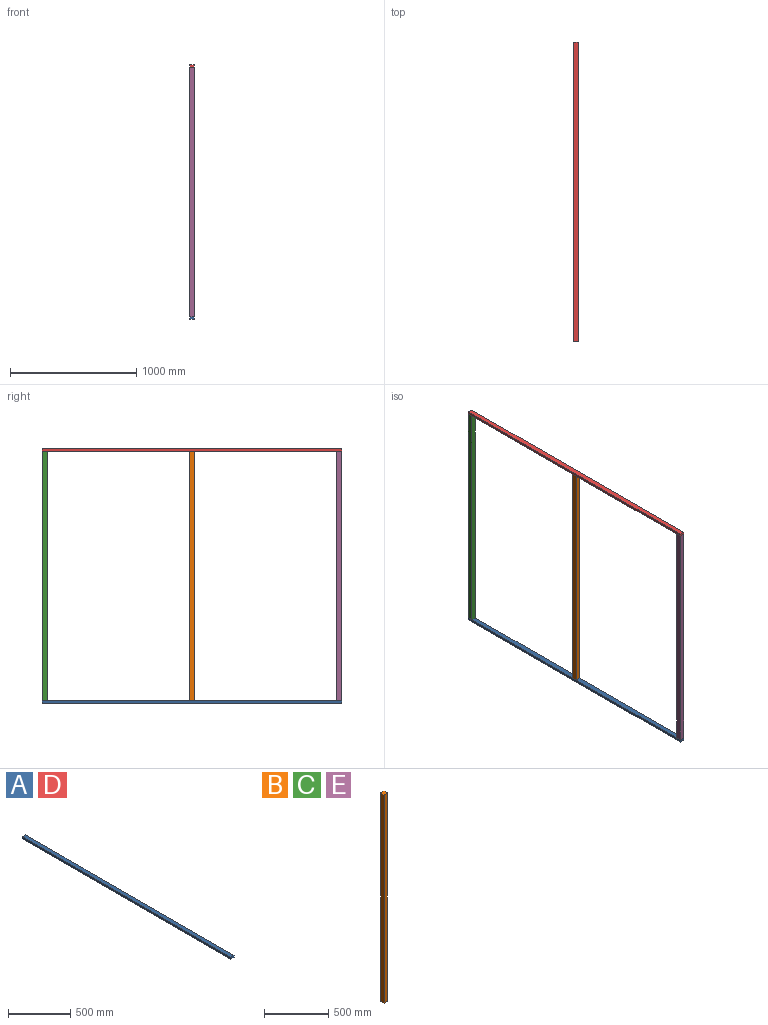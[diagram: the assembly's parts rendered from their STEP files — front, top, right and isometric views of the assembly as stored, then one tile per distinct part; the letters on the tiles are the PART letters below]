
ASSEMBLY  parts=5 mates=4
PART A: 6 faces, bbox 38.1x2374.9x19.1 mm
  f0: plane 38.1x19.05mm, normal (0,-1,0), area 725.8mm2, adj f1,f2,f4,f5
  f1: plane 2374.9x19.05mm, normal (-1,0,0), area 45241.8mm2, adj f0,f2,f3,f4
  f2: plane 2374.9x38.1mm, normal (0,0,1), area 90483.7mm2, adj f0,f1,f3,f5
  f3: plane 38.1x19.05mm, normal (0,1,0), area 725.8mm2, adj f1,f2,f4,f5
  f4: plane 2374.9x38.1mm, normal (0,0,-1), area 90483.7mm2, adj f0,f1,f3,f5
  f5: plane 2374.9x19.05mm, normal (1,0,0), area 45241.8mm2, adj f0,f2,f3,f4
PART B: 6 faces, bbox 38.1x38.1x1981.2 mm
  f0: plane 1981.2x38.1mm, normal (-1,0,0), area 75483.7mm2, adj f1,f3,f4,f5
  f1: plane 1981.2x38.1mm, normal (0,-1,0), area 75483.7mm2, adj f0,f2,f4,f5
  f2: plane 1981.2x38.1mm, normal (1,0,0), area 75483.7mm2, adj f1,f3,f4,f5
  f3: plane 1981.2x38.1mm, normal (0,1,0), area 75483.7mm2, adj f0,f2,f4,f5
  f4: plane 38.1x38.1mm, normal (0,0,1), area 1451.6mm2, adj f0,f1,f2,f3
  f5: plane 38.1x38.1mm, normal (0,0,-1), area 1451.6mm2, adj f0,f1,f2,f3
PART C: same geometry as B
PART D: same geometry as A
PART E: same geometry as B
PLACE A t=(-50.8,31.75,-39.37)mm
PLACE B t=(-50.8,-1136.65,-39.37)mm
PLACE C t=(-50.8,31.75,-39.37)mm
PLACE D t=(-50.8,31.75,1960.88)mm
PLACE E t=(-50.8,-2305.05,-39.37)mm
MATE fastened D.f5 <-> B.f2  axis (1,0,0) through (19.05,-1187.45,2000.25)mm
MATE fastened A.f5 <-> B.f2  axis (1,0,0) through (19.05,-1187.45,19.05)mm
MATE fastened C.f3 <-> A.f3  axis (0,1,0) through (0,0,19.05)mm
MATE fastened A.f0 <-> E.f1  axis (0,-1,0) through (0,-2374.9,19.05)mm
